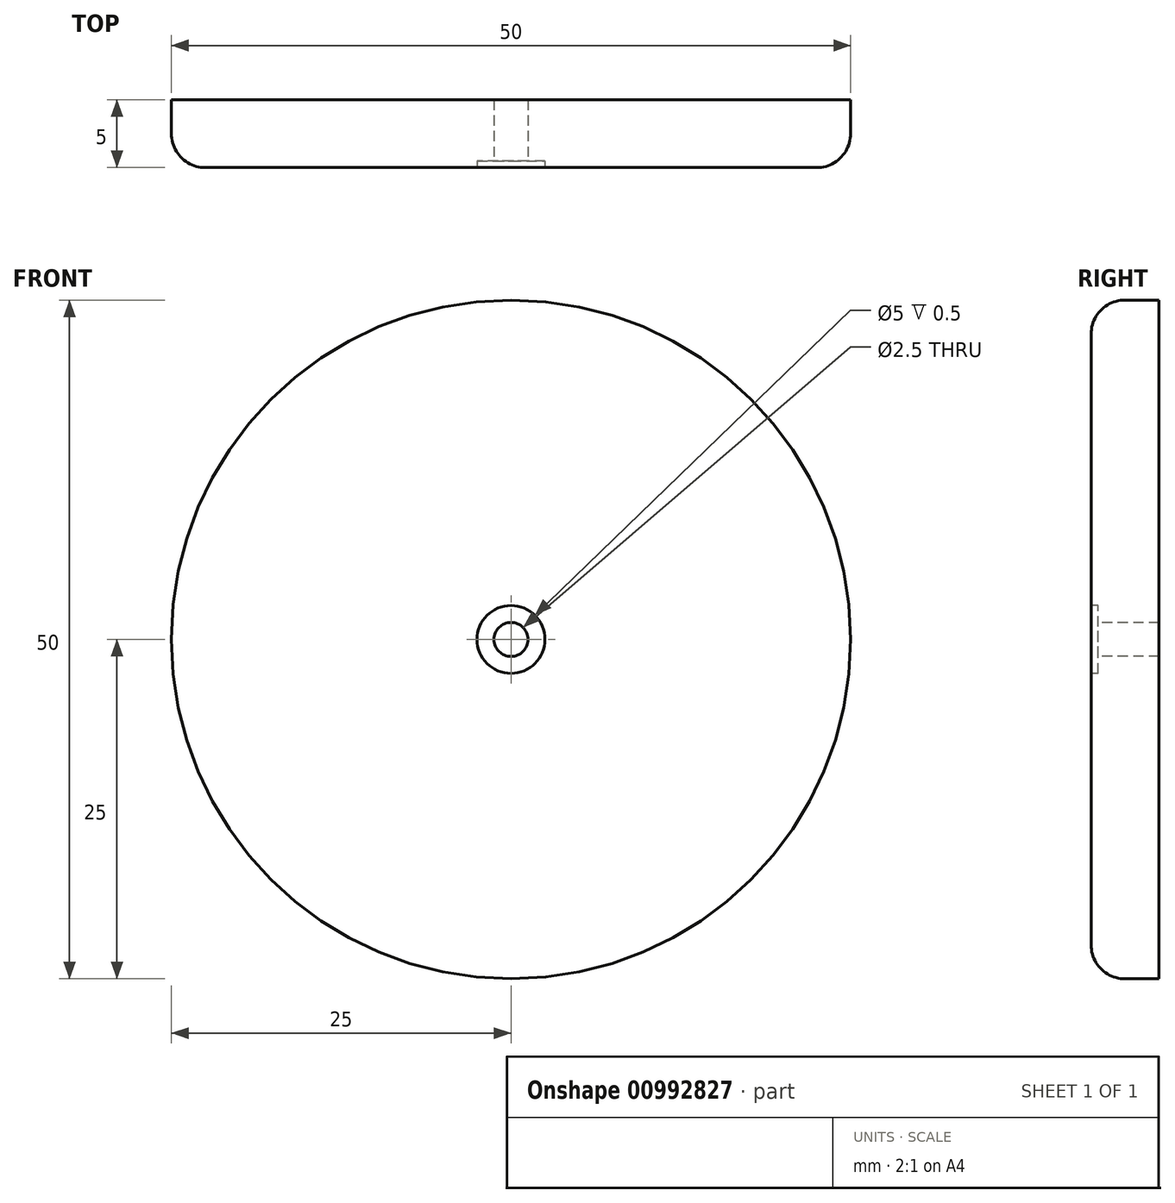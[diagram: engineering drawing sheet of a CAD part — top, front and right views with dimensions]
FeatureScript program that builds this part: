
annotation { "Feature Type Name" : "Feature", "Feature Type Description" : "" }
export const myFeature = defineFeature(function(context is Context, id is Id, definition is map)
    precondition{}
    {
        {
            var Q0;
            Q0=qCreatedBy(makeId("Front.planeOp"),FACE);
            var sketch = newSketch(context, id + "F0", { "sketchPlane" : qUnion([Q0])});
            skCircle(sketch, "E0", {"center": v(0, 0) * mm, "radius": 25 * mm});
            skSolve(sketch);
        }
        {
            var Q0;
            Q0=makeQuery(id+"F0.imprint","IMPRINT",FACE,{"disambiguationData":[TD([[makeQuery(id+"F0.imprint","IMPRINT",EDGE,{"derivedFrom":sQuery(id+"F0.wireOp",EDGE,"E0")}),1.0]])]});
            extrude(context, id + "F1", {"entities" : qUnion([Q0]), "depth" : 5 * mm, "offsetDistance" : 25 * mm});
        }
        {
            var Q0;
            Q0=makeQuery(id+"F1.opExtrude","CAP_EDGE",EDGE,{"disambiguationData":[OSD([sQuery(id+"F0.wireOp",EDGE,"E0")])],"isStart":false});
            fillet(context, id + "F2", {"entities" : qUnion([Q0]), "radius" : 2.5 * mm, "tangentPropagation" : true, "allowEdgeOverflow" : false});
        }
        {
            var Q0;
            Q0=makeQuery(id+"F1.opExtrude","CAP_FACE",FACE,{"disambiguationData":[OSD([sQuery(id+"F0.wireOp",EDGE,"E0")])],"isStart":false});
            var sketch = newSketch(context, id + "F3", { "sketchPlane" : qUnion([Q0])});
            skCircle(sketch, "E1", {"center": v(0, 0) * mm, "radius": 2.5 * mm});
            skCircle(sketch, "E2", {"center": v(0, 0) * mm, "radius": 1.25 * mm});
            skSolve(sketch);
        }
        {
            var Q0;
            Q0=makeQuery(id+"F3.imprint","IMPRINT",FACE,{"disambiguationData":[TD([[makeQuery(id+"F3.imprint","IMPRINT",EDGE,{"derivedFrom":sQuery(id+"F3.wireOp",EDGE,"E1")}),1.0]])]});
            extrude(context, id + "F4", {"entities" : qUnion([Q0]), "operationType" : NewBodyOperationType.REMOVE, "oppositeDirection" : true, "depth" : 0.5 * mm, "offsetDistance" : 25 * mm});
        }
        {
            var Q0;
            Q0=makeQuery(id+"F4.boolean.opBoolean","SPLIT",FACE,{"disambiguationData":[TD([makeQuery(id+"F4.opExtrude","SWEPT_FACE",FACE,{"disambiguationData":[OSD([sQuery(id+"F3.wireOp",EDGE,"E2")])]})])],"derivedFrom":makeQuery(id+"F1.opExtrude","CAP_FACE",FACE,{"disambiguationData":[OSD([sQuery(id+"F0.wireOp",EDGE,"E0")])],"isStart":false})});
            extrude(context, id + "F5", {"entities" : qUnion([Q0]), "operationType" : NewBodyOperationType.REMOVE, "oppositeDirection" : true, "depth" : 32.62 * mm, "offsetDistance" : 25 * mm});
        }
    });
